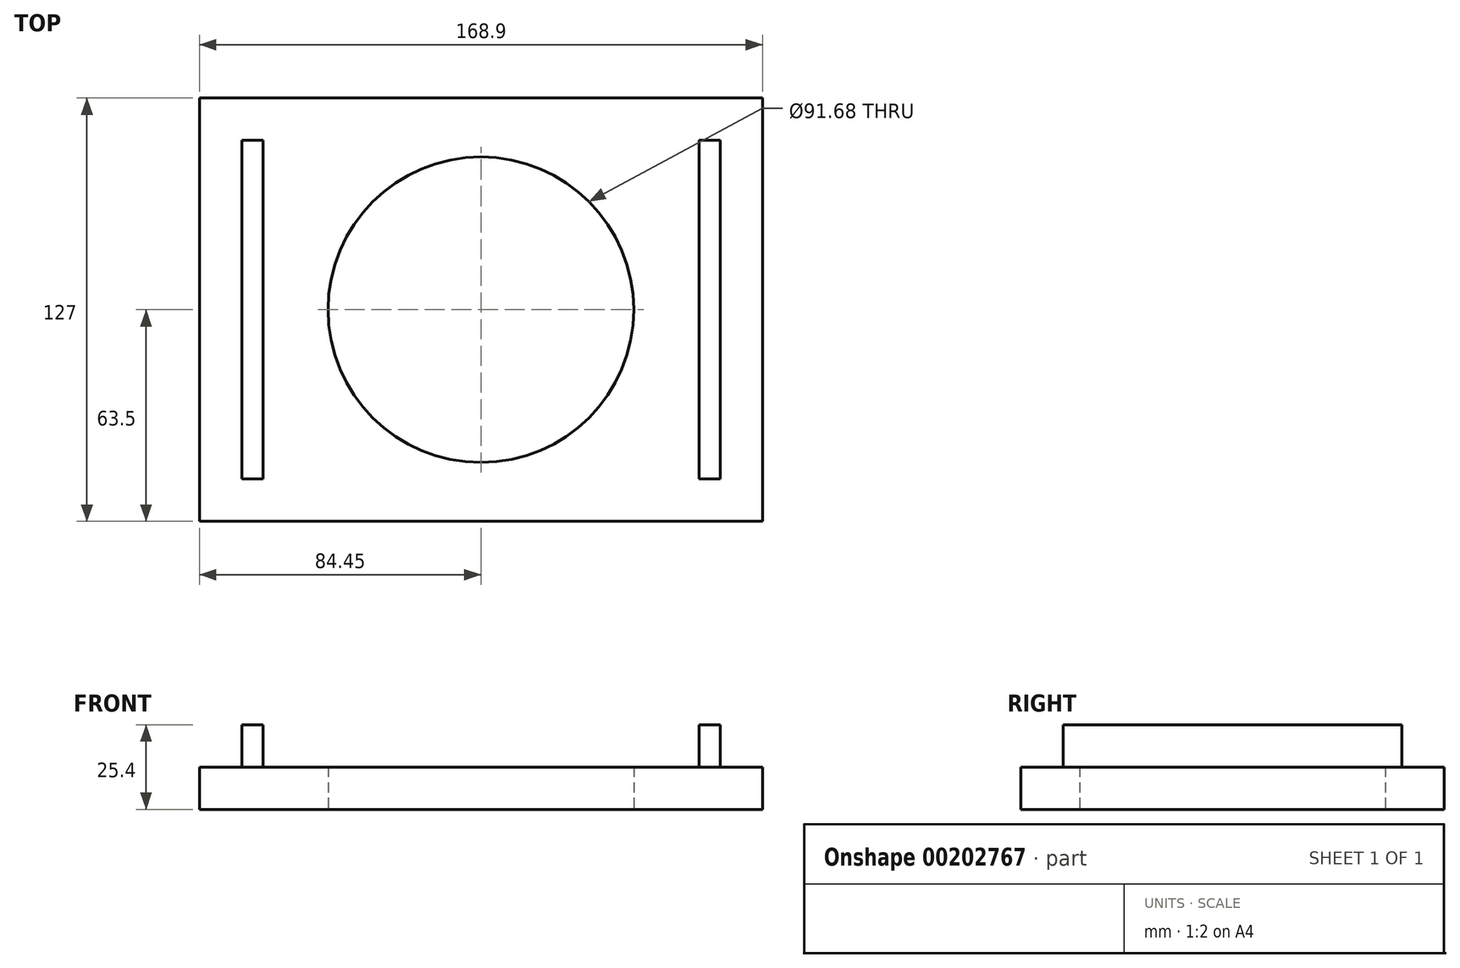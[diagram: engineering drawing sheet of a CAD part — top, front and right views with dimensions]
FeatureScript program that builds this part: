
annotation { "Feature Type Name" : "Feature", "Feature Type Description" : "" }
export const myFeature = defineFeature(function(context is Context, id is Id, definition is map)
    precondition{}
    {
        {
            var Q0;
            Q0=qCreatedBy(makeId("Top.planeOp"),FACE);
            var sketch = newSketch(context, id + "F0", { "sketchPlane" : qUnion([Q0])});
            skLineSegment(sketch, "E0.bottom", {"start": v(-84.45, 63.5) * mm, "end": v(84.46, 63.5) * mm});
            skLineSegment(sketch, "E0.top", {"start": v(-84.46, -63.5) * mm, "end": v(84.45, -63.5) * mm});
            skLineSegment(sketch, "E0.left", {"start": v(-84.45, 63.5) * mm, "end": v(-84.46, -63.5) * mm});
            skLineSegment(sketch, "E0.right", {"start": v(84.46, 63.5) * mm, "end": v(84.45, -63.5) * mm});
            skPoint(sketch, "E0.middle", {"position": v(0, 0) * mm});
            skSolve(sketch);
        }
        {
            var Q0;
            Q0=makeQuery(id+"F0.imprint","IMPRINT",FACE,{"disambiguationData":[TD([[makeQuery(id+"F0.imprint","IMPRINT",EDGE,{"derivedFrom":sQuery(id+"F0.wireOp",EDGE,"E0.bottom")}),-1.0]])]});
            extrude(context, id + "F1", {"entities" : qUnion([Q0]), "depth" : 12.7 * mm});
        }
        {
            var Q0;
            Q0=makeQuery(id+"F1.opExtrude","CAP_FACE",FACE,{"disambiguationData":[OSD([sQuery(id+"F0.wireOp",EDGE,"E0.bottom"),sQuery(id+"F0.wireOp",EDGE,"E0.top"),sQuery(id+"F0.wireOp",EDGE,"E0.left"),sQuery(id+"F0.wireOp",EDGE,"E0.right")])],"isStart":false});
            var sketch = newSketch(context, id + "F2", { "sketchPlane" : qUnion([Q0])});
            skLineSegment(sketch, "E1.bottom", {"start": v(-65.4, 50.8) * mm, "end": v(-71.76, 50.8) * mm});
            skLineSegment(sketch, "E1.top", {"start": v(-65.4, -50.8) * mm, "end": v(-71.76, -50.8) * mm});
            skLineSegment(sketch, "E1.left", {"start": v(-65.4, 50.8) * mm, "end": v(-65.4, -50.8) * mm});
            skLineSegment(sketch, "E1.right", {"start": v(-71.76, 50.8) * mm, "end": v(-71.76, -50.8) * mm});
            skPoint(sketch, "E1.middle", {"position": v(-68.58, 0) * mm});
            skLineSegment(sketch, "E2.bottom", {"start": v(65.4, 50.8) * mm, "end": v(71.76, 50.8) * mm});
            skLineSegment(sketch, "E2.top", {"start": v(65.4, -50.8) * mm, "end": v(71.76, -50.8) * mm});
            skLineSegment(sketch, "E2.left", {"start": v(65.4, 50.8) * mm, "end": v(65.4, -50.8) * mm});
            skLineSegment(sketch, "E2.right", {"start": v(71.76, 50.8) * mm, "end": v(71.76, -50.8) * mm});
            skPoint(sketch, "E2.middle", {"position": v(68.58, 0) * mm});
            skSolve(sketch);
        }
        {
            var Q0;
            Q0=makeQuery(id+"F2.imprint","IMPRINT",FACE,{"disambiguationData":[TD([[makeQuery(id+"F2.imprint","IMPRINT",EDGE,{"derivedFrom":sQuery(id+"F2.wireOp",EDGE,"E2.bottom")}),-1.0]])]});
            var Q1;
            Q1=makeQuery(id+"F2.imprint","IMPRINT",FACE,{"disambiguationData":[TD([[makeQuery(id+"F2.imprint","IMPRINT",EDGE,{"derivedFrom":sQuery(id+"F2.wireOp",EDGE,"E1.bottom")}),1.0]])]});
            extrude(context, id + "F3", {"entities" : qUnion([Q0, Q1]), "operationType" : NewBodyOperationType.ADD, "depth" : 12.7 * mm});
        }
        {
            var Q0;
            Q0=qCreatedBy(makeId("Top.planeOp"),FACE);
            var sketch = newSketch(context, id + "F4", { "sketchPlane" : qUnion([Q0])});
            skCircle(sketch, "E3", {"center": v(0, 0) * mm, "radius": 45.84 * mm});
            skSolve(sketch);
        }
        {
            var Q0;
            Q0 = qSketchRegion(id + "F4", true);
            extrude(context, id + "F5", {"entities" : qUnion([Q0]), "operationType" : NewBodyOperationType.REMOVE, "depth" : 25.4 * mm});
        }
    });
